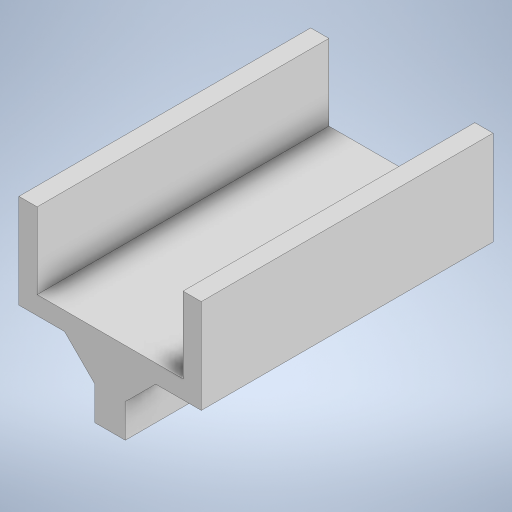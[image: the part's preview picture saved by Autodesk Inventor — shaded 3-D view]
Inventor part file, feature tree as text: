
AUTODESK INVENTOR PART (.ipt)
format: ipt  version: 2024 (Build 280153000, 153)  size: 253,952 bytes
history: native  units: mm
features: extrude x4, projected_geometry x4, other x1, chamfer x1, sketch x1
ambient origin geometry x8: Origin, YZ Plane, XZ Plane, XY Plane, X Axis, Y Axis, Z Axis, Center Point
bodies: Body1 (feature_tree)
feature tree (11):
  other  "솔리드1"
  extrude  "돌출1"  Depth=4.8mm
  extrude  "돌출2"  Depth=9.6mm
  extrude  "돌출3"  Depth=0.6mm TaperAngle=0.0deg
  chamfer  "모따기1"  Distance=0.6mm
  extrude  "돌출4"  Depth=0.6mm
  sketch  "스케치2"
  projected_geometry  "투영된 루프1"
  projected_geometry  "투영된 루프2"
  projected_geometry  "투영된 루프3"
  projected_geometry  "투영된 루프4"
